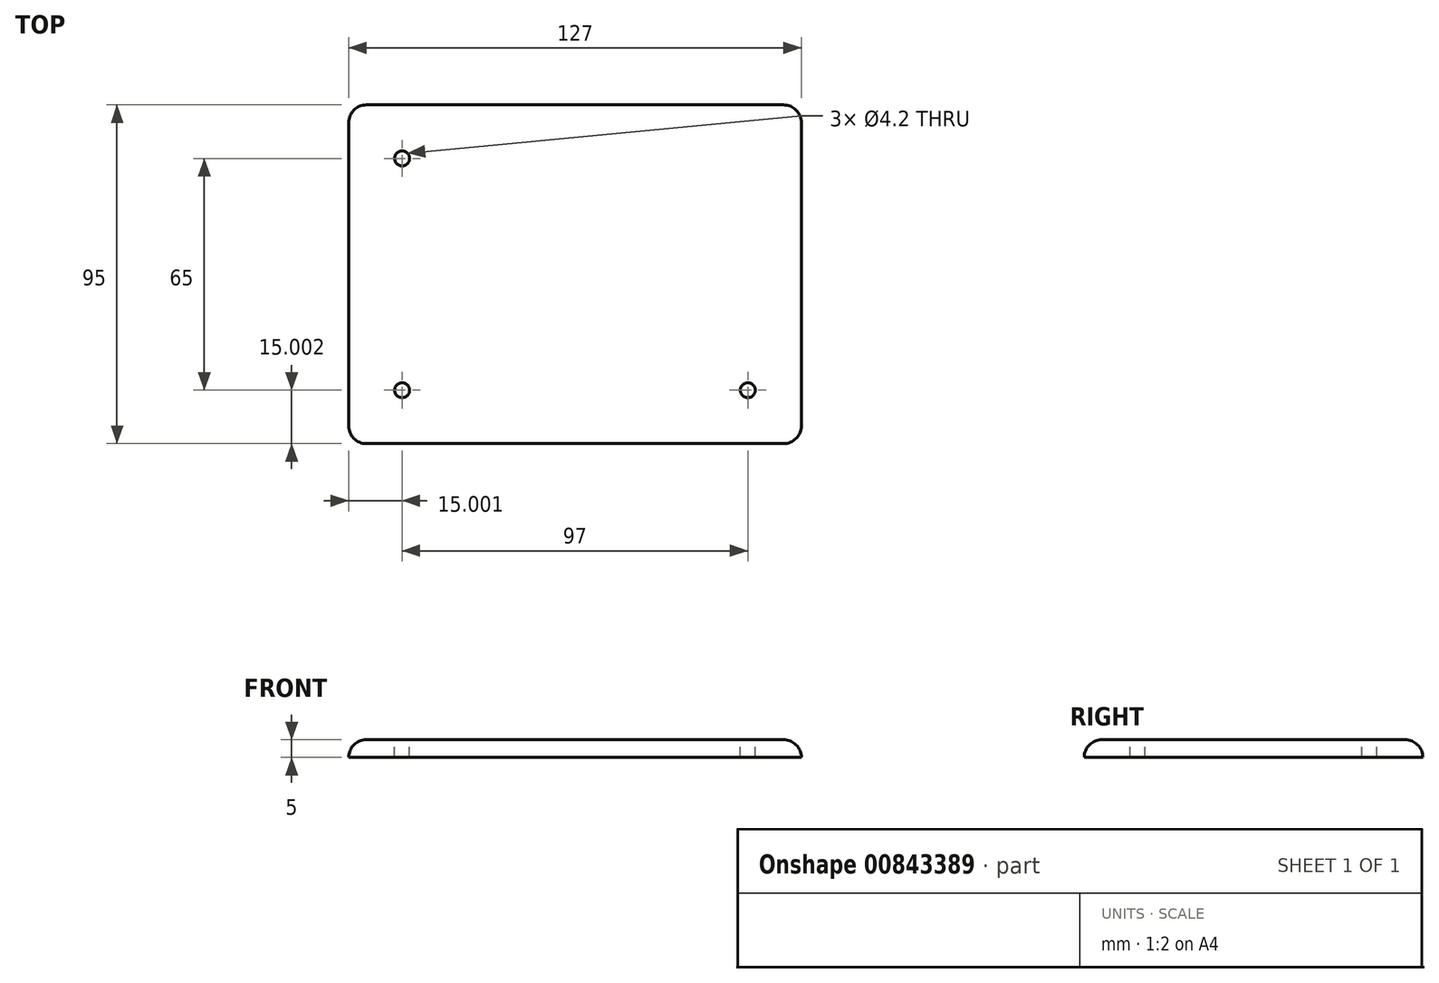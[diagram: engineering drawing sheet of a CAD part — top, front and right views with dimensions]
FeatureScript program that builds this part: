
annotation { "Feature Type Name" : "Feature", "Feature Type Description" : "" }
export const myFeature = defineFeature(function(context is Context, id is Id, definition is map)
    precondition{}
    {
        {
            var Q0;
            Q0=qCreatedBy(makeId("Top.planeOp"),FACE);
            var sketch = newSketch(context, id + "F0", { "sketchPlane" : qUnion([Q0])});
            skLineSegment(sketch, "E0.bottom", {"start": v(-61.97, 47.43) * mm, "end": v(65.03, 47.43) * mm});
            skLineSegment(sketch, "E0.top", {"start": v(-61.97, -47.57) * mm, "end": v(65.03, -47.57) * mm});
            skLineSegment(sketch, "E0.left", {"start": v(-61.97, 47.43) * mm, "end": v(-61.97, -47.57) * mm});
            skLineSegment(sketch, "E0.right", {"start": v(65.03, 47.43) * mm, "end": v(65.03, -47.57) * mm});
            skSolve(sketch);
        }
        {
            var Q0;
            Q0=makeQuery(id+"F0.imprint","IMPRINT",FACE,{"disambiguationData":[TD([[makeQuery(id+"F0.imprint","IMPRINT",EDGE,{"derivedFrom":sQuery(id+"F0.wireOp",EDGE,"E0.bottom")}),-1.0]])]});
            extrude(context, id + "F1", {"entities" : qUnion([Q0]), "depth" : 5 * mm, "offsetDistance" : 25 * mm});
        }
        {
            var Q0;
            Q0=makeQuery(id+"F1.opExtrude","CAP_FACE",FACE,{"disambiguationData":[OSD([sQuery(id+"F0.wireOp",EDGE,"E0.bottom"),sQuery(id+"F0.wireOp",EDGE,"E0.top"),sQuery(id+"F0.wireOp",EDGE,"E0.left"),sQuery(id+"F0.wireOp",EDGE,"E0.right")])],"isStart":false});
            var sketch = newSketch(context, id + "F2", { "sketchPlane" : qUnion([Q0])});
            skCircle(sketch, "E1", {"center": v(-46.97, 32.43) * mm, "radius": 2.1 * mm});
            skCircle(sketch, "E2", {"center": v(-46.97, -32.57) * mm, "radius": 2.1 * mm});
            skCircle(sketch, "E3", {"center": v(50.03, -32.57) * mm, "radius": 2.1 * mm});
            skSolve(sketch);
        }
        {
            var Q0;
            Q0=makeQuery(id+"F2.imprint","IMPRINT",FACE,{"disambiguationData":[TD([[makeQuery(id+"F2.imprint","IMPRINT",EDGE,{"derivedFrom":sQuery(id+"F2.wireOp",EDGE,"E1")}),1.0]])]});
            var Q1;
            Q1=makeQuery(id+"F2.imprint","IMPRINT",FACE,{"disambiguationData":[TD([[makeQuery(id+"F2.imprint","IMPRINT",EDGE,{"derivedFrom":sQuery(id+"F2.wireOp",EDGE,"E2")}),1.0]])]});
            var Q2;
            Q2=makeQuery(id+"F2.imprint","IMPRINT",FACE,{"disambiguationData":[TD([[makeQuery(id+"F2.imprint","IMPRINT",EDGE,{"derivedFrom":sQuery(id+"F2.wireOp",EDGE,"E3")}),1.0]])]});
            extrude(context, id + "F3", {"entities" : qUnion([Q0, Q1, Q2]), "operationType" : NewBodyOperationType.REMOVE, "endBound" : BoundingType.THROUGH_ALL, "oppositeDirection" : true, "depth" : 25 * mm, "offsetDistance" : 25 * mm});
        }
        {
            var Q0;
            Q0=makeQuery(id+"F1.opExtrude","CAP_EDGE",EDGE,{"disambiguationData":[OSD([sQuery(id+"F0.wireOp",EDGE,"E0.bottom")])],"isStart":false});
            var Q1;
            Q1=makeQuery(id+"F1.opExtrude","CAP_EDGE",EDGE,{"disambiguationData":[OSD([sQuery(id+"F0.wireOp",EDGE,"E0.right")])],"isStart":false});
            var Q2;
            Q2=makeQuery(id+"F1.opExtrude","CAP_EDGE",EDGE,{"disambiguationData":[OSD([sQuery(id+"F0.wireOp",EDGE,"E0.left")])],"isStart":false});
            var Q3;
            Q3=makeQuery(id+"F1.opExtrude","CAP_EDGE",EDGE,{"disambiguationData":[OSD([sQuery(id+"F0.wireOp",EDGE,"E0.top")])],"isStart":false});
            var Q4;
            Q4=makeQuery(id+"F1.opExtrude","SWEPT_EDGE",EDGE,{"disambiguationData":[OSD([sQuery(id+"F0.wireOp",EDGE,"E0.top"),sQuery(id+"F0.wireOp",EDGE,"E0.left")])]});
            var Q5;
            Q5=makeQuery(id+"F1.opExtrude","SWEPT_EDGE",EDGE,{"disambiguationData":[OSD([sQuery(id+"F0.wireOp",EDGE,"E0.bottom"),sQuery(id+"F0.wireOp",EDGE,"E0.left")])]});
            var Q6;
            Q6=makeQuery(id+"F1.opExtrude","SWEPT_EDGE",EDGE,{"disambiguationData":[OSD([sQuery(id+"F0.wireOp",EDGE,"E0.bottom"),sQuery(id+"F0.wireOp",EDGE,"E0.right")])]});
            var Q7;
            Q7=makeQuery(id+"F1.opExtrude","SWEPT_EDGE",EDGE,{"disambiguationData":[OSD([sQuery(id+"F0.wireOp",EDGE,"E0.top"),sQuery(id+"F0.wireOp",EDGE,"E0.right")])]});
            fillet(context, id + "F4", {"entities" : qUnion([Q0, Q1, Q2, Q3, Q4, Q5, Q6, Q7]), "radius" : 5 * mm, "tangentPropagation" : true, "allowEdgeOverflow" : false});
        }
    });
